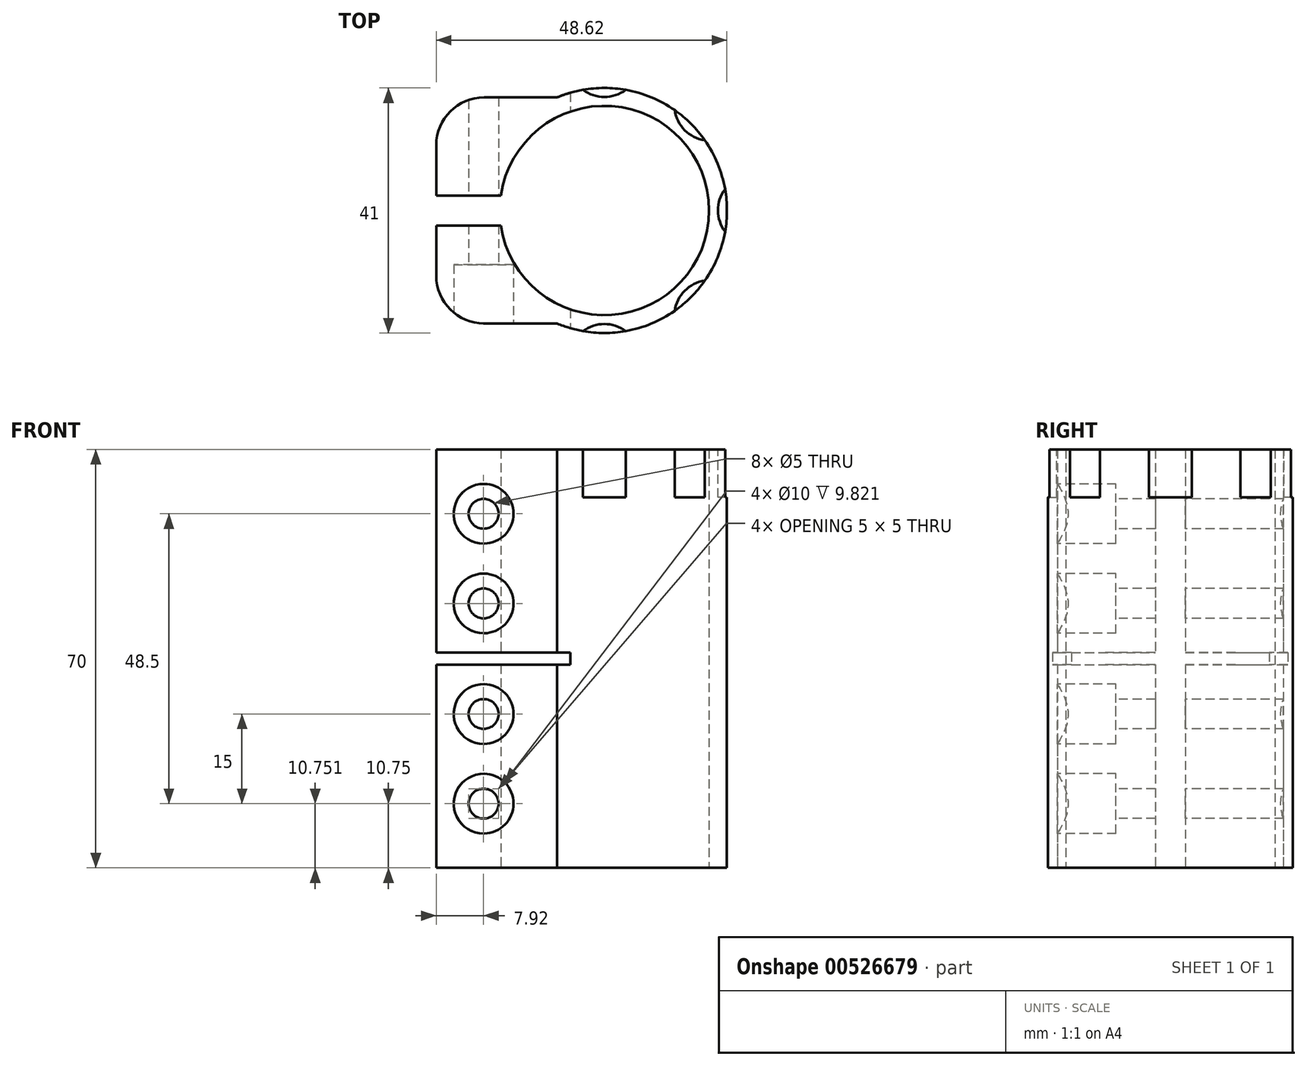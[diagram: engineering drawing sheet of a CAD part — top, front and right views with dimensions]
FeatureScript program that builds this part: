
annotation { "Feature Type Name" : "Feature", "Feature Type Description" : "" }
export const myFeature = defineFeature(function(context is Context, id is Id, definition is map)
    precondition{}
    {
        {
            var Q0;
            Q0=qCreatedBy(makeId("Top.planeOp"),FACE);
            var sketch = newSketch(context, id + "F0", { "sketchPlane" : qUnion([Q0])});
            skArc(sketch, "E0", {"start": v(-17.32, -2.5) * mm, "mid": v(17.5, 0) * mm, "end": v(-17.32, 2.5) * mm});
            skArc(sketch, "E1", {"start": v(-7.92, -18.9) * mm, "mid": v(20.5, 0) * mm, "end": v(-7.92, 18.9) * mm});
            skLineSegment(sketch, "E2", {"start": v(-7.92, 18.9) * mm, "end": v(-20.12, 18.9) * mm});
            skLineSegment(sketch, "E3", {"start": v(-28.12, 10.9) * mm, "end": v(-28.12, 2.5) * mm});
            skLineSegment(sketch, "E4", {"start": v(-28.12, 2.5) * mm, "end": v(-17.32, 2.5) * mm});
            skPoint(sketch, "E5.visualSharp", {"position": v(-28.12, 18.9) * mm});
            skArc(sketch, "E5.filletArc", {"start": v(-20.12, 18.9) * mm, "mid": v(-25.78, 16.57) * mm, "end": v(-28.12, 10.9) * mm});
            skLineSegment(sketch, "E6", {"start": v(0, 0) * mm, "end": v(45.27, 0) * mm, "construction": true});
            skLineSegment(sketch, "E7.MirrorCS", {"start": v(-28.12, -2.5) * mm, "end": v(-17.32, -2.5) * mm});
            skLineSegment(sketch, "E8.MirrorCS", {"start": v(-7.92, -18.9) * mm, "end": v(-20.12, -18.9) * mm});
            skLineSegment(sketch, "E9.MirrorCS", {"start": v(-28.12, -10.9) * mm, "end": v(-28.12, -2.5) * mm});
            skArc(sketch, "E10.MirrorCS", {"start": v(-20.12, -18.9) * mm, "mid": v(-25.78, -16.57) * mm, "end": v(-28.12, -10.9) * mm});
            skPoint(sketch, "E11.orphan", {"position": v(-17.32, -2.5) * mm});
            skSolve(sketch);
        }
        {
            var Q0;
            Q0 = qSketchRegion(id + "F0", true);
            extrude(context, id + "F1", {"entities" : qUnion([Q0]), "depth" : 70 * mm, "offsetDistance" : 25 * mm, "symmetric" : true});
        }
        {
            var Q0;
            Q0=makeQuery(id+"F1.opExtrude","SWEPT_FACE",FACE,{"disambiguationData":[OSD([sQuery(id+"F0.wireOp",EDGE,"E8.MirrorCS")])]});
            var sketch = newSketch(context, id + "F2", { "sketchPlane" : qUnion([Q0])});
            skPoint(sketch, "E12", {"position": v(-20.2, -24.25) * mm});
            skPoint(sketch, "E13", {"position": v(-20.2, -9.25) * mm});
            skPoint(sketch, "E14", {"position": v(-20.2, 9.25) * mm});
            skPoint(sketch, "E15", {"position": v(-20.2, 24.25) * mm});
            skSolve(sketch);
        }
        {
            var Q0;
            Q0=sQuery(id+"F2.wireOp",VERTEX,"E12");
            var Q1;
            Q1=sQuery(id+"F2.wireOp",VERTEX,"E13");
            var Q2;
            Q2=sQuery(id+"F2.wireOp",VERTEX,"E14");
            var Q3;
            Q3=sQuery(id+"F2.wireOp",VERTEX,"E15");
            var Q4;
            Q4=makeQuery(id+"F1.opExtrude","SWEPT_BODY",BODY,{"disambiguationData":[OSD([sQuery(id+"F0.wireOp",EDGE,"E0"),sQuery(id+"F0.wireOp",EDGE,"E1"),sQuery(id+"F0.wireOp",EDGE,"E2"),sQuery(id+"F0.wireOp",EDGE,"E3"),sQuery(id+"F0.wireOp",EDGE,"E4"),sQuery(id+"F0.wireOp",EDGE,"E5.filletArc"),sQuery(id+"F0.wireOp",EDGE,"E7.MirrorCS"),sQuery(id+"F0.wireOp",EDGE,"E8.MirrorCS"),sQuery(id+"F0.wireOp",EDGE,"E9.MirrorCS"),sQuery(id+"F0.wireOp",EDGE,"E10.MirrorCS")])]});
            hole(context, id + "F3", {"style" : HoleStyle.C_BORE, "endStyle" : HoleEndStyle.THROUGH, "holeDiameter" : 5 * mm, "cBoreDiameter" : 10 * mm, "cBoreDepth" : 8 * mm, "majorDiameter" : 5 * mm, "isTappedThrough" : true, "tappedDepth" : 12 * mm, "tapClearance" : 3, "locations" : qUnion([Q0, Q1, Q2, Q3]), "scope" : qUnion([Q4])});
        }
        {
            var Q0;
            Q0=qCreatedBy(makeId("Front.planeOp"),FACE);
            var sketch = newSketch(context, id + "F4", { "sketchPlane" : qUnion([Q0])});
            skLineSegment(sketch, "E16.bottom", {"start": v(-28.12, 1) * mm, "end": v(-5.72, 1) * mm});
            skLineSegment(sketch, "E16.top", {"start": v(-28.12, -1) * mm, "end": v(-5.72, -1) * mm});
            skLineSegment(sketch, "E16.left", {"start": v(-28.12, 1) * mm, "end": v(-28.12, -1) * mm});
            skLineSegment(sketch, "E16.right", {"start": v(-5.72, 1) * mm, "end": v(-5.72, -1) * mm});
            skSolve(sketch);
        }
        {
            var Q0;
            Q0 = qSketchRegion(id + "F4", true);
            extrude(context, id + "F5", {"entities" : qUnion([Q0]), "operationType" : NewBodyOperationType.REMOVE, "oppositeDirection" : true, "depth" : 50 * mm, "offsetDistance" : 25 * mm, "symmetric" : true});
        }
        {
            var Q0;
            Q0=makeQuery(id+"F1.opExtrude","CAP_FACE",FACE,{"disambiguationData":[OSD([sQuery(id+"F0.wireOp",EDGE,"E0"),sQuery(id+"F0.wireOp",EDGE,"E1"),sQuery(id+"F0.wireOp",EDGE,"E2"),sQuery(id+"F0.wireOp",EDGE,"E3"),sQuery(id+"F0.wireOp",EDGE,"E4"),sQuery(id+"F0.wireOp",EDGE,"E5.filletArc"),sQuery(id+"F0.wireOp",EDGE,"E7.MirrorCS"),sQuery(id+"F0.wireOp",EDGE,"E8.MirrorCS"),sQuery(id+"F0.wireOp",EDGE,"E9.MirrorCS"),sQuery(id+"F0.wireOp",EDGE,"E10.MirrorCS")])],"isStart":false});
            var sketch = newSketch(context, id + "F6", { "sketchPlane" : qUnion([Q0])});
            skCircle(sketch, "E17", {"center": v(0, -25) * mm, "radius": 6 * mm});
            skCircle(sketch, "E18.1.0", {"center": v(17.68, -17.68) * mm, "radius": 6 * mm});
            skCircle(sketch, "E18.2.0", {"center": v(25, 0) * mm, "radius": 6 * mm});
            skCircle(sketch, "E18.3.0", {"center": v(17.68, 17.68) * mm, "radius": 6 * mm});
            skCircle(sketch, "E18.4.0", {"center": v(0, 25) * mm, "radius": 6 * mm});
            skPoint(sketch, "E18.center", {"position": v(0, 0) * mm});
            skLineSegment(sketch, "E18.anchor1", {"start": v(0, 0) * mm, "end": v(0, -25) * mm, "construction": true});
            skLineSegment(sketch, "E18.anchor2", {"start": v(0, 0) * mm, "end": v(0, 25) * mm, "construction": true});
            skSolve(sketch);
        }
        {
            var Q0;
            Q0 = qSketchRegion(id + "F6", true);
            extrude(context, id + "F7", {"entities" : qUnion([Q0]), "operationType" : NewBodyOperationType.REMOVE, "oppositeDirection" : true, "depth" : 8 * mm, "offsetDistance" : 25 * mm});
        }
    });
